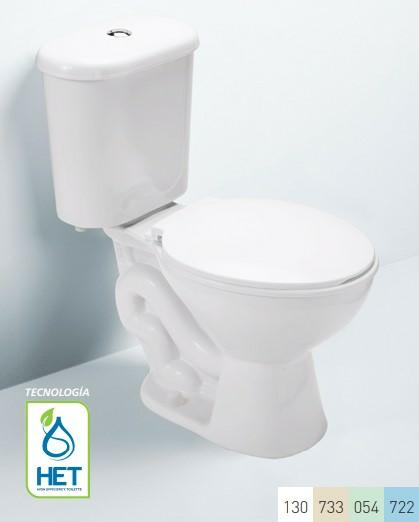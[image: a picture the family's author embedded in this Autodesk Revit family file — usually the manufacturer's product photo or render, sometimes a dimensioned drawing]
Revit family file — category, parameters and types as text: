
# Revit family: BRG-GRF-CCN_BELA MONOMANDO COCINA PULL OUT CROMO v_02
name_source: partatom
category: Aparatos sanitarios
units: mm (PartAtom-declared; Revit-internal decimal feet)

## family parameters
Compartido = Sí
Corte con vacíos al cargar = No
Cota de conector redondo = Diámetro de uso
Número OmniClass = 23.45.00.00
Punto de cálculo de habitación = Sí
Se basa en plano de trabajo = No
Siempre vertical = Sí
Tipo de pieza = Normal
Título OmniClass = Sanitary, Laundry, and Cleaning Equipment

## types (1)
- BELA MONOMANDO PULL OUT PARA COCINA
    Conexión AC = Sí
    Conexión AF = Sí
    Conexión de residuos = Sí
    Conexión de ventilación = Sí
    Fabricante = EDESA Ecuador
    Imagen de tipo = <Ninguno>
    Modelo = BELA MONOMANDO PULL OUT PARA COCINA
    URL = https://www.briggs.com.ec
    _ALT_Basamento = 0.85 m
    _ALT_Eje instalación = 0.6 m
    _EDESA_ Alto en cm = 27.9
    _EDESA_ Ancho en cm = 12.1
    _EDESA_ Categoría = Productos > Grifería > Cocina
    _EDESA_ Certificación = Cumple con norma NTE - INEN 3123 basada en la norma ASME 112.18.1 - 2012. Nuestras mangueras cuentan certificación cUPC.
    _EDESA_ Color = Cromo
    _EDESA_ Conexión hidráulica = Entrada de agua: tubería ø 1/2" Salida de agua: tubería PVC 50
    _EDESA_ Consumo/capacidad de agua en L = 8.3 litros por minuto / 2.2 gpm a 60 psi
    _EDESA_ Descripción = Grifería monomando de cocina pull out para agua fría y caliente. Instalación sobre fregadero o mesón. Incluye mangueras flexibles.
    _EDESA_ Distancia de instalación en cm (muro terminado) = 0
    _EDESA_ Garantía = De por vida para el cuerpo principal y acabado en cromo (306)
    _EDESA_ Marca = BRIGGS
    _EDESA_ Materiales = Latón
    _EDESA_ Nombre = BELA MONOMANDO PULL OUT PARA COCINA
    _EDESA_ Peso en kg = 0
    _EDESA_ Productos incluídos = 2 Mangueras monomando 16"
    _EDESA_ Productos necesarios para instalación = Desagüe y Sifón para fregadero
    _EDESA_ Profundidad en cm = 23
    _EDESA_ Página web = https://www.briggs.com.ec
    _EDESA_ Sku/código = SG0087093061CW
    _EDESA_ Tipo de instalación = Sobre fregadero o mesón
